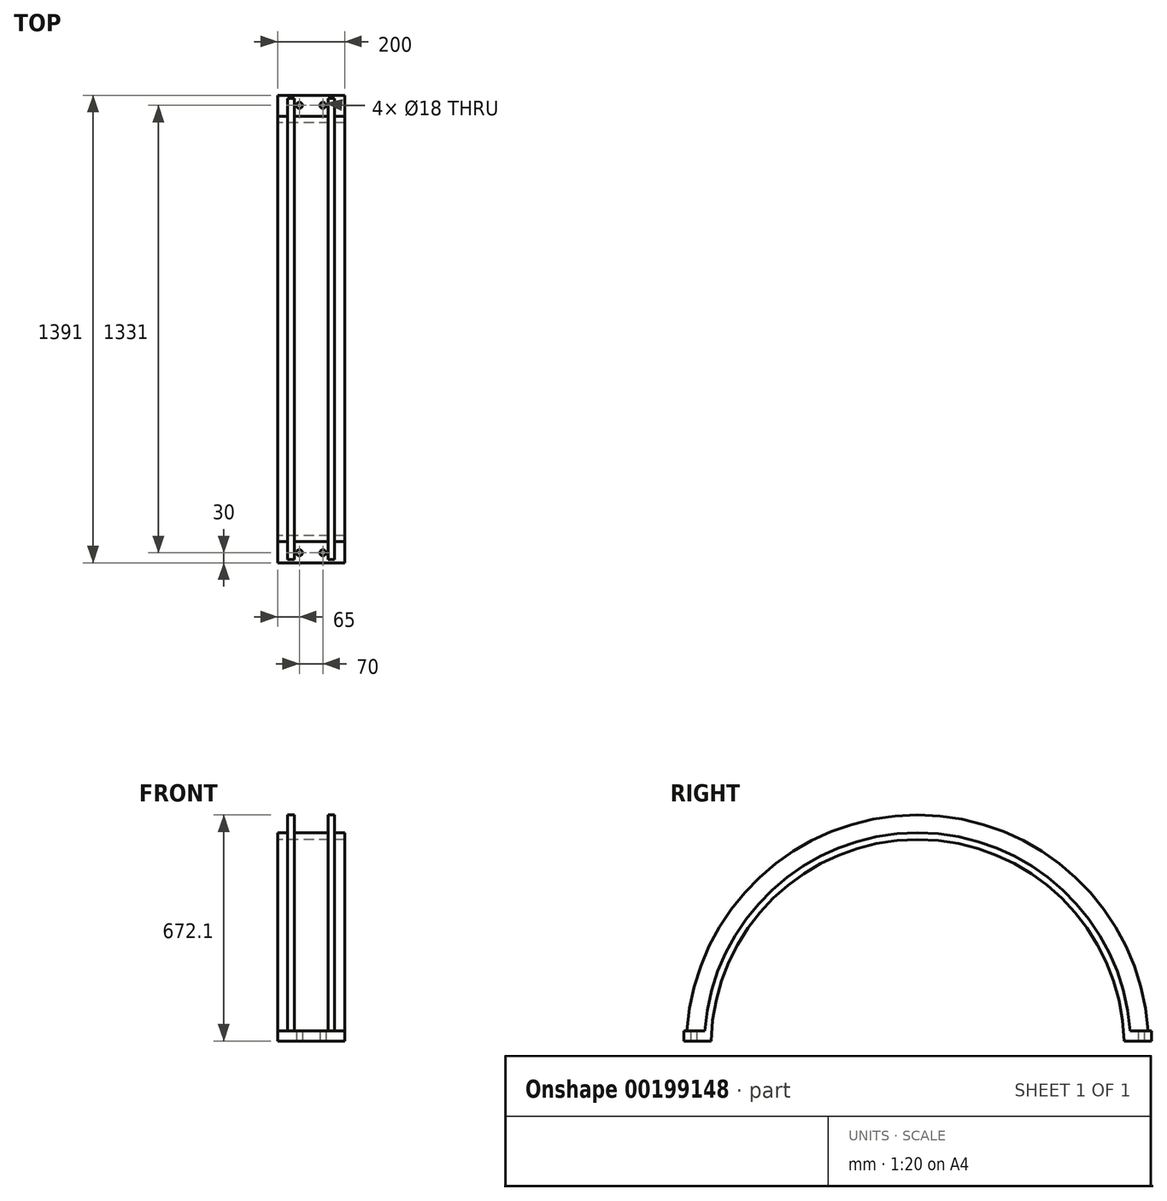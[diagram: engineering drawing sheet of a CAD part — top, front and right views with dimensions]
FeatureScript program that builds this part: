
annotation { "Feature Type Name" : "Feature", "Feature Type Description" : "" }
export const myFeature = defineFeature(function(context is Context, id is Id, definition is map)
    precondition{}
    {
        {
            var Q0;
            Q0=qCreatedBy(makeId("Right.planeOp"),FACE);
            var sketch = newSketch(context, id + "F0", { "sketchPlane" : qUnion([Q0])});
            skArc(sketch, "E0", {"start": v(613.92, 15) * mm, "mid": v(0, 614.1) * mm, "end": v(-613.92, 15) * mm});
            skLineSegment(sketch, "E1", {"start": v(-614.1, 0) * mm, "end": v(614.1, 0) * mm, "construction": true});
            skLineSegment(sketch, "E2", {"start": v(-613.92, 15) * mm, "end": v(613.92, 15) * mm, "construction": true});
            skArc(sketch, "E3", {"start": v(633.92, 15) * mm, "mid": v(0, 634.1) * mm, "end": v(-633.92, 15) * mm});
            skLineSegment(sketch, "E4", {"start": v(-613.92, 15) * mm, "end": v(-633.92, 15) * mm});
            skLineSegment(sketch, "E5", {"start": v(613.92, 15) * mm, "end": v(633.92, 15) * mm});
            skSolve(sketch);
        }
        {
            var Q0;
            Q0 = qSketchRegion(id + "F0", true);
            extrude(context, id + "F1", {"entities" : qUnion([Q0]), "endBound" : BoundingType.SYMMETRIC, "depth" : 200 * mm});
        }
        {
            var Q0;
            Q0=makeQuery(id+"F1.opExtrude","CAP_FACE",FACE,{"disambiguationData":[OSD([sQuery(id+"F0.wireOp",EDGE,"E0"),sQuery(id+"F0.wireOp",EDGE,"E3"),sQuery(id+"F0.wireOp",EDGE,"E4"),sQuery(id+"F0.wireOp",EDGE,"E5")])],"isStart":false});
            cPlane(context, id + "F2", {"entities" : qUnion([Q0]), "cplaneType" : CPlaneType.OFFSET, "offset" : 30 * mm, "oppositeDirection" : true, "width" : 150 * mm, "height" : 150 * mm});
        }
        {
            var Q0;
            Q0=qCreatedBy(id+"F2.planeOp",FACE);
            var sketch = newSketch(context, id + "F3", { "sketchPlane" : qUnion([Q0])});
            skArc(sketch, "E6.0", {"start": v(633.92, 15) * mm, "mid": v(0, 634.1) * mm, "end": v(-633.92, 15) * mm});
            skLineSegment(sketch, "E7", {"start": v(-686.94, 15) * mm, "end": v(-633.92, 15) * mm});
            skLineSegment(sketch, "E8.trimOffspring", {"start": v(633.92, 15) * mm, "end": v(686.94, 15) * mm});
            skArc(sketch, "E9", {"start": v(686.94, 15) * mm, "mid": v(0, 687.1) * mm, "end": v(-686.94, 15) * mm});
            skSolve(sketch);
        }
        {
            var Q0;
            Q0=makeQuery(id+"F3.imprint","IMPRINT",FACE,{"disambiguationData":[TD([[makeQuery(id+"F3.imprint","IMPRINT",EDGE,{"derivedFrom":sQuery(id+"F3.wireOp",EDGE,"E6.0")}),-1.0]])]});
            extrude(context, id + "F4", {"entities" : qUnion([Q0]), "operationType" : NewBodyOperationType.ADD, "oppositeDirection" : true, "depth" : 20 * mm});
        }
        {
            var Q0;
            Q0=makeQuery(id+"F1.opExtrude","CAP_FACE",FACE,{"disambiguationData":[OSD([sQuery(id+"F0.wireOp",EDGE,"E0"),sQuery(id+"F0.wireOp",EDGE,"E3"),sQuery(id+"F0.wireOp",EDGE,"E4"),sQuery(id+"F0.wireOp",EDGE,"E5")])],"isStart":true});
            cPlane(context, id + "F5", {"entities" : qUnion([Q0]), "cplaneType" : CPlaneType.OFFSET, "offset" : 30 * mm, "oppositeDirection" : true, "width" : 150 * mm, "height" : 150 * mm});
        }
        {
            var Q0;
            Q0=qCreatedBy(id+"F5.planeOp",FACE);
            var sketch = newSketch(context, id + "F6", { "sketchPlane" : qUnion([Q0])});
            skArc(sketch, "E10.0", {"start": v(-633.92, 15) * mm, "mid": v(0, 634.1) * mm, "end": v(633.92, 15) * mm});
            skArc(sketch, "E11.0", {"start": v(-686.94, 15) * mm, "mid": v(0, 687.1) * mm, "end": v(686.94, 15) * mm});
            skLineSegment(sketch, "E12.0", {"start": v(-633.92, 15) * mm, "end": v(-686.94, 15) * mm});
            skLineSegment(sketch, "E12.1", {"start": v(686.94, 15) * mm, "end": v(633.92, 15) * mm});
            skSolve(sketch);
        }
        {
            var Q0;
            Q0 = qSketchRegion(id + "F6", true);
            extrude(context, id + "F7", {"entities" : qUnion([Q0]), "operationType" : NewBodyOperationType.ADD, "oppositeDirection" : true, "depth" : 20 * mm});
        }
        {
            var Q0;
            Q0=makeQuery(id+"F7.boolean.opBoolean","MERGE",FACE,{"derivedFrom":[makeQuery(id+"F4.boolean.opBoolean","MERGE",FACE,{"derivedFrom":[makeQuery(id+"F1.opExtrude","SWEPT_FACE",FACE,{"disambiguationData":[OSD([sQuery(id+"F0.wireOp",EDGE,"E4")])]}),makeQuery(id+"F4.opExtrude","SWEPT_FACE",FACE,{"disambiguationData":[OSD([sQuery(id+"F3.wireOp",EDGE,"E7")])]})]}),makeQuery(id+"F7.opExtrude","SWEPT_FACE",FACE,{"disambiguationData":[OSD([sQuery(id+"F6.wireOp",EDGE,"E12.1")])]})]});
            var sketch = newSketch(context, id + "F8", { "sketchPlane" : qUnion([Q0])});
            skLineSegment(sketch, "E13.bottom", {"start": v(-100, 613.92) * mm, "end": v(100, 613.92) * mm});
            skLineSegment(sketch, "E13.top", {"start": v(-100, 695.5) * mm, "end": v(100, 695.5) * mm});
            skLineSegment(sketch, "E13.left", {"start": v(-100, 613.92) * mm, "end": v(-100, 695.5) * mm});
            skLineSegment(sketch, "E13.right", {"start": v(100, 613.92) * mm, "end": v(100, 695.5) * mm});
            skLineSegment(sketch, "E14", {"start": v(-100, 0) * mm, "end": v(100, 0) * mm, "construction": true});
            skLineSegment(sketch, "E15.MirrorCS", {"start": v(-100, -695.5) * mm, "end": v(100, -695.5) * mm});
            skLineSegment(sketch, "E16.MirrorCS", {"start": v(-100, -613.92) * mm, "end": v(100, -613.92) * mm});
            skLineSegment(sketch, "E17.MirrorCS", {"start": v(-100, -613.92) * mm, "end": v(-100, -695.5) * mm});
            skLineSegment(sketch, "E18.MirrorCS", {"start": v(100, -613.92) * mm, "end": v(100, -695.5) * mm});
            skSolve(sketch);
        }
        {
            var Q0;
            Q0=makeQuery(id+"F8.imprint","IMPRINT",FACE,{"disambiguationData":[TD([[makeQuery(id+"F8.imprint","IMPRINT",EDGE,{"derivedFrom":sQuery(id+"F8.wireOp",EDGE,"E15.MirrorCS")}),1.0]])]});
            var Q1;
            {var subQ15=sQuery(id+"F8.wireOp",EDGE,"E13.top");Q1=makeQuery(id+"F8.imprint","IMPRINT",FACE,{"disambiguationData":[TD([[makeQuery(id+"F8.imprint","IMPRINT",EDGE,{"derivedFrom":subQ15}),-1.0]])]});}
            var Q2;
            {var subQ16=sQuery(id+"F8.wireOp",EDGE,"E13.bottom");Q2=makeQuery(id+"F8.imprint","IMPRINT",FACE,{"disambiguationData":[TD([[makeQuery(id+"F8.imprint","IMPRINT",EDGE,{"derivedFrom":subQ16}),-1.0]])]});}
            extrude(context, id + "F9", {"entities" : qUnion([Q0, Q1, Q2]), "operationType" : NewBodyOperationType.ADD, "oppositeDirection" : true, "depth" : 30 * mm});
        }
        {
            var Q0;
            Q0=makeQuery(id+"F9.boolean.opBoolean","MERGE",FACE,{"derivedFrom":[makeQuery(id+"F7.boolean.opBoolean","MERGE",FACE,{"derivedFrom":[makeQuery(id+"F4.boolean.opBoolean","MERGE",FACE,{"derivedFrom":[makeQuery(id+"F1.opExtrude","SWEPT_FACE",FACE,{"disambiguationData":[OSD([sQuery(id+"F0.wireOp",EDGE,"E5")])]}),makeQuery(id+"F4.opExtrude","SWEPT_FACE",FACE,{"disambiguationData":[OSD([sQuery(id+"F3.wireOp",EDGE,"E8.trimOffspring")])]})]}),makeQuery(id+"F7.opExtrude","SWEPT_FACE",FACE,{"disambiguationData":[OSD([sQuery(id+"F6.wireOp",EDGE,"E12.0")])]})]}),makeQuery(id+"F9.opExtrude","CAP_FACE",FACE,{"disambiguationData":[OSD([sQuery(id+"F8.wireOp",EDGE,"E15.MirrorCS"),sQuery(id+"F8.wireOp",EDGE,"E16.MirrorCS"),sQuery(id+"F8.wireOp",EDGE,"E17.MirrorCS"),sQuery(id+"F8.wireOp",EDGE,"E18.MirrorCS")])],"isStart":true})]});
            var sketch = newSketch(context, id + "F10", { "sketchPlane" : qUnion([Q0])});
            skLineSegment(sketch, "E19", {"start": v(-35, 665.5) * mm, "end": v(35, 665.5) * mm, "construction": true});
            skCircle(sketch, "E20", {"center": v(-35, 665.5) * mm, "radius": 9 * mm});
            skCircle(sketch, "E21", {"center": v(35, 665.5) * mm, "radius": 9 * mm});
            skLineSegment(sketch, "E22", {"start": v(0, 665.5) * mm, "end": v(0, 695.5) * mm});
            skLineSegment(sketch, "E23", {"start": v(-100, 0) * mm, "end": v(100, 0) * mm, "construction": true});
            skCircle(sketch, "E24.MirrorC", {"center": v(-35, -665.5) * mm, "radius": 9 * mm});
            skCircle(sketch, "E25.MirrorC", {"center": v(35, -665.5) * mm, "radius": 9 * mm});
            skSolve(sketch);
        }
        {
            var Q0;
            Q0 = qSketchRegion(id + "F10", true);
            extrude(context, id + "F11", {"entities" : qUnion([Q0]), "operationType" : NewBodyOperationType.REMOVE, "endBound" : BoundingType.THROUGH_ALL, "oppositeDirection" : true, "depth" : 25 * mm});
        }
    });
